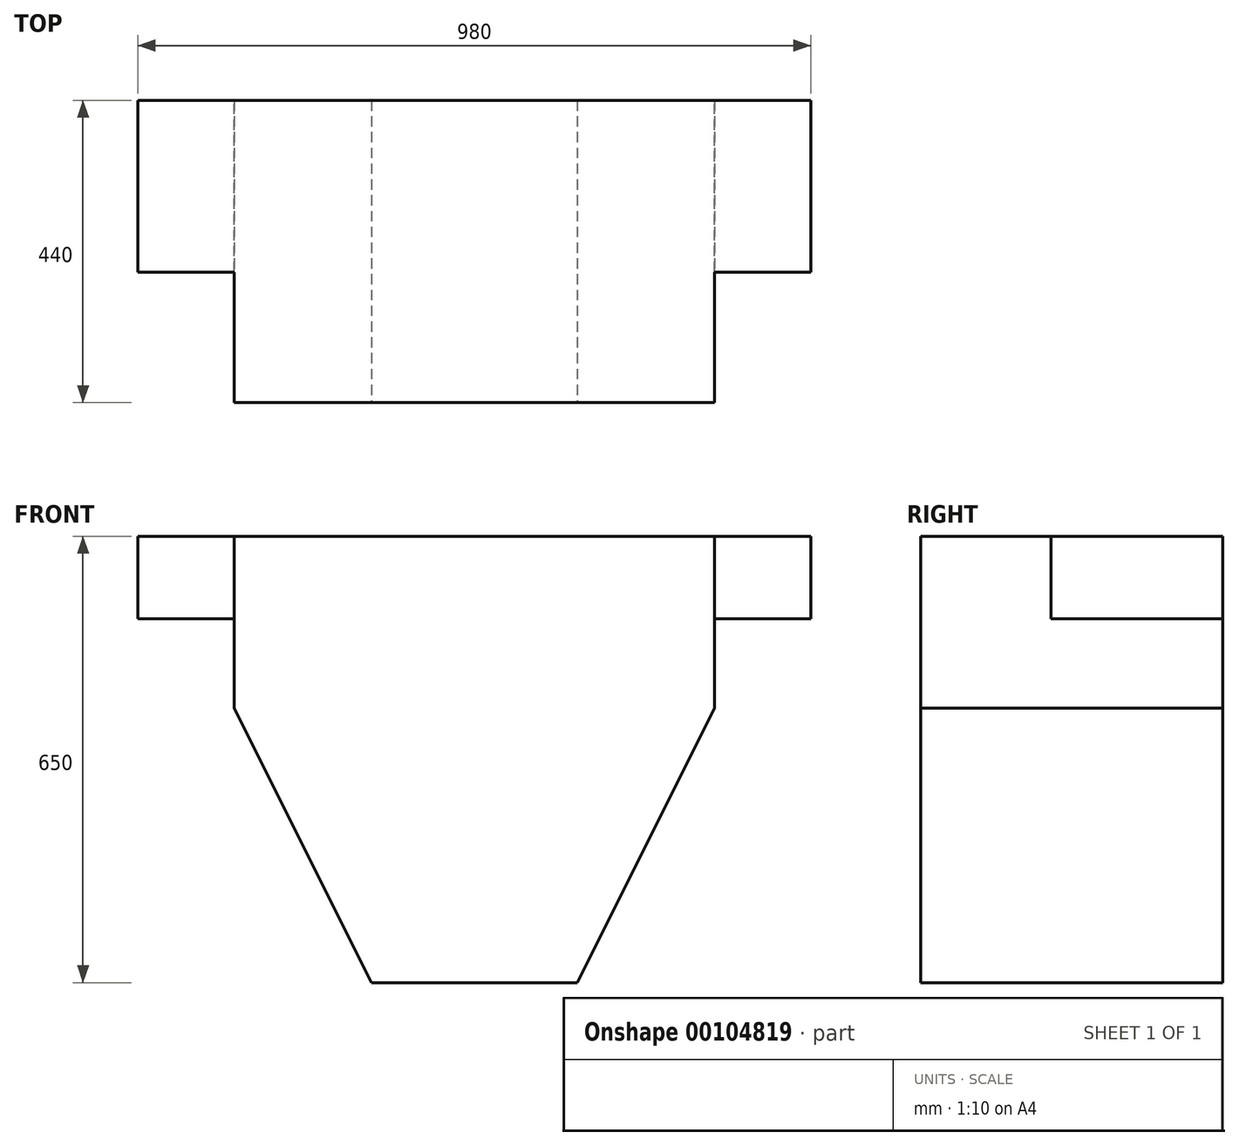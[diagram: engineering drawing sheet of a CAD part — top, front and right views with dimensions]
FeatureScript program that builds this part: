
annotation { "Feature Type Name" : "Feature", "Feature Type Description" : "" }
export const myFeature = defineFeature(function(context is Context, id is Id, definition is map)
    precondition{}
    {
        {
            var Q0;
            Q0=qCreatedBy(makeId("Front.planeOp"),FACE);
            var sketch = newSketch(context, id + "F0", { "sketchPlane" : qUnion([Q0])});
            skLineSegment(sketch, "E0.bottom", {"start": v(350, 325) * mm, "end": v(-350, 325) * mm});
            skLineSegment(sketch, "E0.top", {"start": v(350, -325) * mm, "end": v(-350, -325) * mm});
            skLineSegment(sketch, "E0.left", {"start": v(350, 325) * mm, "end": v(350, -325) * mm});
            skLineSegment(sketch, "E0.right", {"start": v(-350, 325) * mm, "end": v(-350, -325) * mm});
            skPoint(sketch, "E0.middle", {"position": v(0, 0) * mm});
            skSolve(sketch);
        }
        {
            var Q0;
            Q0 = qSketchRegion(id + "F0", true);
            extrude(context, id + "F1", {"entities" : qUnion([Q0]), "depth" : 440 * mm});
        }
        {
            var Q0;
            Q0=makeQuery(id+"F1.opExtrude","CAP_FACE",FACE,{"disambiguationData":[OSD([sQuery(id+"F0.wireOp",EDGE,"E0.bottom"),sQuery(id+"F0.wireOp",EDGE,"E0.top"),sQuery(id+"F0.wireOp",EDGE,"E0.left"),sQuery(id+"F0.wireOp",EDGE,"E0.right")])],"isStart":false});
            var sketch = newSketch(context, id + "F2", { "sketchPlane" : qUnion([Q0])});
            skPoint(sketch, "E1", {"position": v(-350, -325) * mm});
            skPoint(sketch, "E2", {"position": v(-350, 75) * mm});
            skPoint(sketch, "E3", {"position": v(350, 75) * mm});
            skPoint(sketch, "E4", {"position": v(350, -325) * mm});
            skPoint(sketch, "E5", {"position": v(-150, -325) * mm});
            skPoint(sketch, "E6", {"position": v(150, -325) * mm});
            skLineSegment(sketch, "E7", {"start": v(-350, 75) * mm, "end": v(-350, -325) * mm});
            skLineSegment(sketch, "E8", {"start": v(-150, -325) * mm, "end": v(-350, -325) * mm});
            skLineSegment(sketch, "E9", {"start": v(-350, 75) * mm, "end": v(-150, -325) * mm});
            skLineSegment(sketch, "E10", {"start": v(150, -325) * mm, "end": v(350, 75) * mm});
            skLineSegment(sketch, "E11", {"start": v(350, 75) * mm, "end": v(350, -325) * mm});
            skLineSegment(sketch, "E12", {"start": v(350, -325) * mm, "end": v(150, -325) * mm});
            skSolve(sketch);
        }
        {
            var Q0;
            Q0 = qSketchRegion(id + "F2", true);
            extrude(context, id + "F3", {"entities" : qUnion([Q0]), "operationType" : NewBodyOperationType.REMOVE, "endBound" : BoundingType.THROUGH_ALL, "oppositeDirection" : true, "depth" : 25 * mm});
        }
        {
            var Q0;
            Q0=makeQuery(id+"F1.opExtrude","SWEPT_FACE",FACE,{"disambiguationData":[OSD([sQuery(id+"F0.wireOp",EDGE,"E0.bottom")])]});
            var sketch = newSketch(context, id + "F4", { "sketchPlane" : qUnion([Q0])});
            skPoint(sketch, "E13", {"position": v(350, 0) * mm});
            skPoint(sketch, "E14", {"position": v(350, -250) * mm});
            skPoint(sketch, "E15", {"position": v(-350, 0) * mm});
            skPoint(sketch, "E16", {"position": v(-350, -250) * mm});
            skLineSegment(sketch, "E17", {"start": v(350, 0) * mm, "end": v(490, 0) * mm});
            skLineSegment(sketch, "E18", {"start": v(490, 0) * mm, "end": v(490, -250) * mm});
            skLineSegment(sketch, "E19", {"start": v(490, -250) * mm, "end": v(350, -250) * mm});
            skLineSegment(sketch, "E20", {"start": v(-350, 0) * mm, "end": v(-490, 0) * mm});
            skLineSegment(sketch, "E21", {"start": v(-490, 0) * mm, "end": v(-490, -250) * mm});
            skLineSegment(sketch, "E22", {"start": v(-490, -250) * mm, "end": v(-350, -250) * mm});
            skLineSegment(sketch, "E23", {"start": v(-350, 0) * mm, "end": v(-350, -250) * mm});
            skLineSegment(sketch, "E24", {"start": v(350, 0) * mm, "end": v(350, -250) * mm});
            skSolve(sketch);
        }
        {
            var Q0;
            Q0 = qSketchRegion(id + "F4", true);
            extrude(context, id + "F5", {"entities" : qUnion([Q0]), "operationType" : NewBodyOperationType.ADD, "oppositeDirection" : true, "depth" : 120 * mm});
        }
    });
